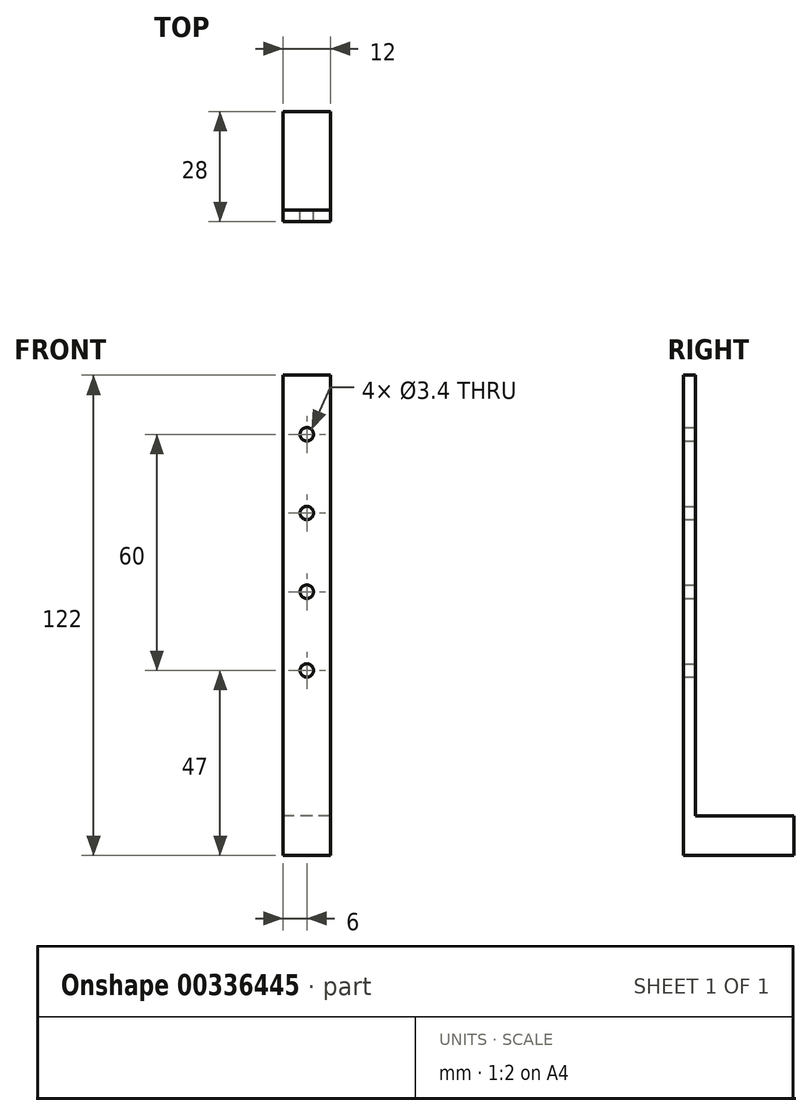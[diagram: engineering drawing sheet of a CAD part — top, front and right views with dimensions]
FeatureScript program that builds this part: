
annotation { "Feature Type Name" : "Feature", "Feature Type Description" : "" }
export const myFeature = defineFeature(function(context is Context, id is Id, definition is map)
    precondition{}
    {
        {
            var Q0;
            Q0=qCreatedBy(makeId("Right.planeOp"),FACE);
            var sketch = newSketch(context, id + "F0", { "sketchPlane" : qUnion([Q0])});
            skLineSegment(sketch, "E0.bottom", {"start": v(0, 0) * mm, "end": v(-3, 0) * mm});
            skLineSegment(sketch, "E0.top", {"start": v(0, 122) * mm, "end": v(-3, 122) * mm});
            skLineSegment(sketch, "E0.left", {"start": v(0, 0) * mm, "end": v(0, 122) * mm});
            skLineSegment(sketch, "E0.right", {"start": v(-3, 0) * mm, "end": v(-3, 122) * mm});
            skSolve(sketch);
        }
        {
            var Q0;
            Q0 = qSketchRegion(id + "F0", true);
            extrude(context, id + "F1", {"entities" : qUnion([Q0]), "depth" : 12 * mm});
        }
        {
            var Q0;
            Q0=makeQuery(id+"F1.opExtrude","SWEPT_FACE",FACE,{"disambiguationData":[OSD([sQuery(id+"F0.wireOp",EDGE,"E0.left")])]});
            var sketch = newSketch(context, id + "F2", { "sketchPlane" : qUnion([Q0])});
            skLineSegment(sketch, "E1.bottom", {"start": v(-12, 0) * mm, "end": v(0, 0) * mm});
            skLineSegment(sketch, "E1.top", {"start": v(-12, 10) * mm, "end": v(0, 10) * mm});
            skLineSegment(sketch, "E1.left", {"start": v(-12, 0) * mm, "end": v(-12, 10) * mm});
            skLineSegment(sketch, "E1.right", {"start": v(0, 0) * mm, "end": v(0, 10) * mm});
            skSolve(sketch);
        }
        {
            var Q0;
            Q0 = qSketchRegion(id + "F2", true);
            extrude(context, id + "F3", {"entities" : qUnion([Q0]), "operationType" : NewBodyOperationType.ADD, "depth" : 25 * mm});
        }
        {
            var Q0;
            Q0=makeQuery(id+"F1.opExtrude","SWEPT_FACE",FACE,{"disambiguationData":[OSD([sQuery(id+"F0.wireOp",EDGE,"E0.left")])]});
            var sketch = newSketch(context, id + "F4", { "sketchPlane" : qUnion([Q0])});
            skCircle(sketch, "E2", {"center": v(-6, 107) * mm, "radius": 1.7 * mm});
            skPoint(sketch, "E2.centerSnap0", {"position": v(-6, 122) * mm});
            skCircle(sketch, "E3", {"center": v(-6, 87) * mm, "radius": 1.7 * mm});
            skCircle(sketch, "E4", {"center": v(-6, 67) * mm, "radius": 1.7 * mm});
            skCircle(sketch, "E5", {"center": v(-6, 47) * mm, "radius": 1.7 * mm});
            skLineSegment(sketch, "E6", {"start": v(-6, 107) * mm, "end": v(-6, 87) * mm, "construction": true});
            skLineSegment(sketch, "E7", {"start": v(-6, 67) * mm, "end": v(-6, 87) * mm, "construction": true});
            skLineSegment(sketch, "E8", {"start": v(-6, 67) * mm, "end": v(-6, 47) * mm, "construction": true});
            skSolve(sketch);
        }
        {
            var Q0;
            Q0 = qSketchRegion(id + "F4", true);
            extrude(context, id + "F5", {"entities" : qUnion([Q0]), "operationType" : NewBodyOperationType.REMOVE, "endBound" : BoundingType.THROUGH_ALL, "oppositeDirection" : true, "depth" : 25 * mm});
        }
    });
